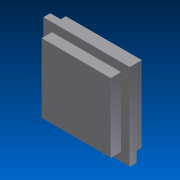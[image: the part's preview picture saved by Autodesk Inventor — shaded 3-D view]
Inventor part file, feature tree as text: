
AUTODESK INVENTOR PART (.ipt)
format: ipt  version: 2012 (Build 160160000, 160)  size: 93,696 bytes
history: native  units: in
note: dims shown in document units (in); Inventor stores cm internally (conversion verified against a paired STEP export)
features: extrude x3, sketch x3
ambient origin geometry x8: Origin, YZ Plane, XZ Plane, XY Plane, X Axis, Y Axis, Z Axis, Center Point
bodies: Solid1 (feature_tree)
feature tree (6):
  extrude  "Extrusion1"  Depth=0.9843in
  extrude  "Extrusion2"  Depth=0.7874in
  extrude  "Extrusion3"  Depth=0.0984in
  sketch  "Sketch1"  dims[d0=0.9843in d1=0.9843in]
  sketch  "Sketch2"  dims[d2=0.0787in d3=0.0in d4=0.7874in]
  sketch  "Sketch3"  dims[d5=0.7874in d6=0.0984in d7=0.0984in d8=0.1181in d9=0.0in d10=0.8661in d11=0.8661in d12=0.0591in d13=0.0591in d14=0.1181in d15=0.0in]
